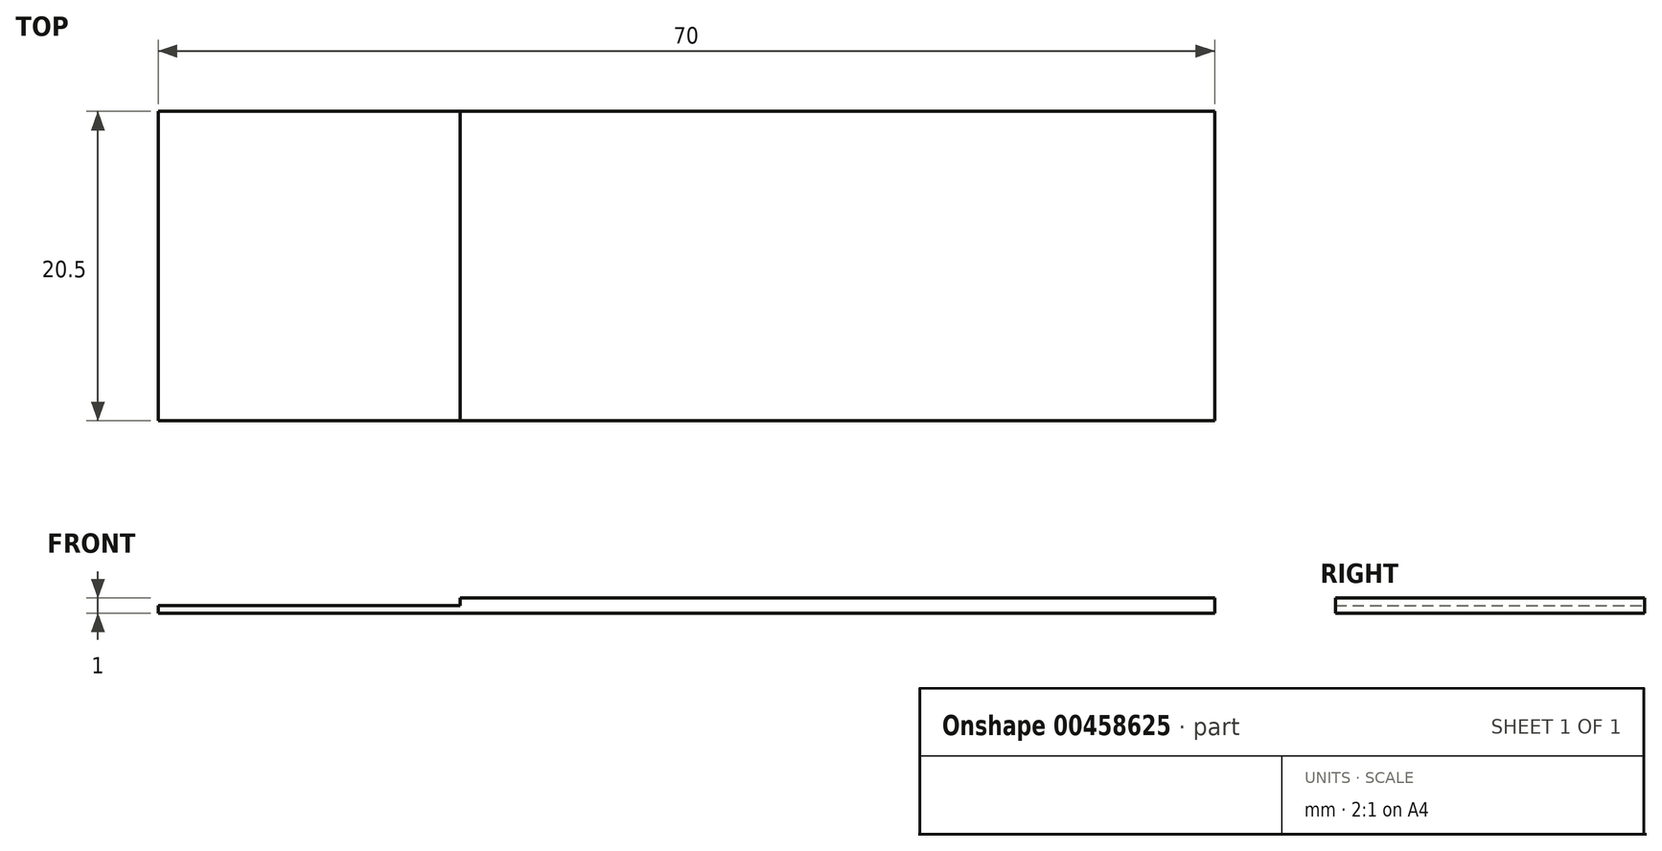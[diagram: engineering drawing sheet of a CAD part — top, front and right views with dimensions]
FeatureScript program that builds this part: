
annotation { "Feature Type Name" : "Feature", "Feature Type Description" : "" }
export const myFeature = defineFeature(function(context is Context, id is Id, definition is map)
    precondition{}
    {
        {
            var Q0;
            Q0=qCreatedBy(makeId("Top.planeOp"),FACE);
            var sketch = newSketch(context, id + "F0", { "sketchPlane" : qUnion([Q0])});
            skLineSegment(sketch, "E0.bottom", {"start": v(35, -10.25) * mm, "end": v(-35, -10.25) * mm});
            skLineSegment(sketch, "E0.top", {"start": v(35, 10.25) * mm, "end": v(-35, 10.25) * mm});
            skLineSegment(sketch, "E0.left", {"start": v(35, -10.25) * mm, "end": v(35, 10.25) * mm});
            skLineSegment(sketch, "E0.right", {"start": v(-35, -10.25) * mm, "end": v(-35, 10.25) * mm});
            skPoint(sketch, "E0.middle", {"position": v(0, 0) * mm});
            skSolve(sketch);
        }
        {
            var Q0;
            Q0=makeQuery(id+"F0.imprint","IMPRINT",FACE,{"disambiguationData":[TD([[makeQuery(id+"F0.imprint","IMPRINT",EDGE,{"derivedFrom":sQuery(id+"F0.wireOp",EDGE,"E0.bottom")}),-1.0]])]});
            extrude(context, id + "F1", {"entities" : qUnion([Q0]), "depth" : 1 * mm});
        }
        {
            var Q0;
            Q0=makeQuery(id+"F1.opExtrude","CAP_FACE",FACE,{"disambiguationData":[OSD([sQuery(id+"F0.wireOp",EDGE,"E0.bottom"),sQuery(id+"F0.wireOp",EDGE,"E0.top"),sQuery(id+"F0.wireOp",EDGE,"E0.left"),sQuery(id+"F0.wireOp",EDGE,"E0.right")])],"isStart":false});
            var sketch = newSketch(context, id + "F2", { "sketchPlane" : qUnion([Q0])});
            skLineSegment(sketch, "E1.bottom", {"start": v(-35, 10.25) * mm, "end": v(-15, 10.25) * mm});
            skLineSegment(sketch, "E1.top", {"start": v(-35, -10.25) * mm, "end": v(-15, -10.25) * mm});
            skLineSegment(sketch, "E1.left", {"start": v(-35, 10.25) * mm, "end": v(-35, -10.25) * mm});
            skLineSegment(sketch, "E1.right", {"start": v(-15, 10.25) * mm, "end": v(-15, -10.25) * mm});
            skSolve(sketch);
        }
        {
            var Q0;
            Q0=makeQuery(id+"F2.imprint","IMPRINT",FACE,{"disambiguationData":[TD([[makeQuery(id+"F2.imprint","IMPRINT",EDGE,{"derivedFrom":sQuery(id+"F2.wireOp",EDGE,"E1.bottom")}),1.0]])]});
            extrude(context, id + "F3", {"entities" : qUnion([Q0]), "operationType" : NewBodyOperationType.REMOVE, "oppositeDirection" : true, "depth" : .5 * mm});
        }
    });
